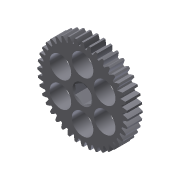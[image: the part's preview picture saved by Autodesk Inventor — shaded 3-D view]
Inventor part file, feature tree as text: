
AUTODESK INVENTOR PART (.ipt)
format: ipt  version: 2011 (Build 150239000, 239)  size: 377,344 bytes
history: native  units: mm (DEFAULTED — no unit token found)
features: sketch x5, other x4, plane x4, extrude x3, revolve x1, mirror x1, pattern_circular x1, projected_geometry x1
ambient origin geometry x8: Origin, YZ Plane, XZ Plane, XY Plane, X Axis, Y Axis, Z Axis, Center Point
bodies: Solid1 (feature_tree)
feature tree (20):
  other  "Gear 40T 20dp 375hex"
  extrude  "Extrusion1"  Depth=8.763mm TaperAngle=0.0deg
  plane  "Work Plane1"
  plane  "Work Plane2"
  plane  "Work Plane3"
  other  "Spur Gear"
  extrude  "Extrusion5"  Depth=76.2mm TaperAngle=0.0deg
  revolve  "Revolution2"  [1 undecoded]
  plane  "Work Plane4"
  mirror  "Mirror1"
  extrude  "Extrusion6"  TaperAngle=0.0deg  [1 undecoded]
  pattern_circular  "Circular Pattern2"  [2 undecoded]
  sketch  "Sketch1"  dims[d0=53.34mm d1=8.763mm d2=0.0mm]
  sketch  "Sketch2"  dims[d3=50.8mm d4=76.2mm d5=0.0mm]
  other  "Srf1"
  sketch  "Sketch7"  dims[d6=0.0mm d7=0.785398mm d9=0.0mm]
  sketch  "Sketch8"  dims[d14=0.0mm d15=127.0mm d16=0.0mm]
  sketch  "Sketch9"  dims[d17=0.0mm d18=0.0mm d19=127.0mm d38=9.525mm d39=25.4mm d40=0.0mm d41=5.9182mm d42=5.070181mm d43=2.54mm d44=90.0deg d45=12.7mm d46=15.08125mm d47=25.4mm d48=0.0mm d49=60.0mm d50=360.0deg]
  other  "Pitch Diameter"
  projected_geometry  "Project Cut Edges2"
note: 4 required parameter values undecoded (feature->parameter linkage not recoverable at this tier; creation-order binding heuristic only, values carry confidence <= 0.55)